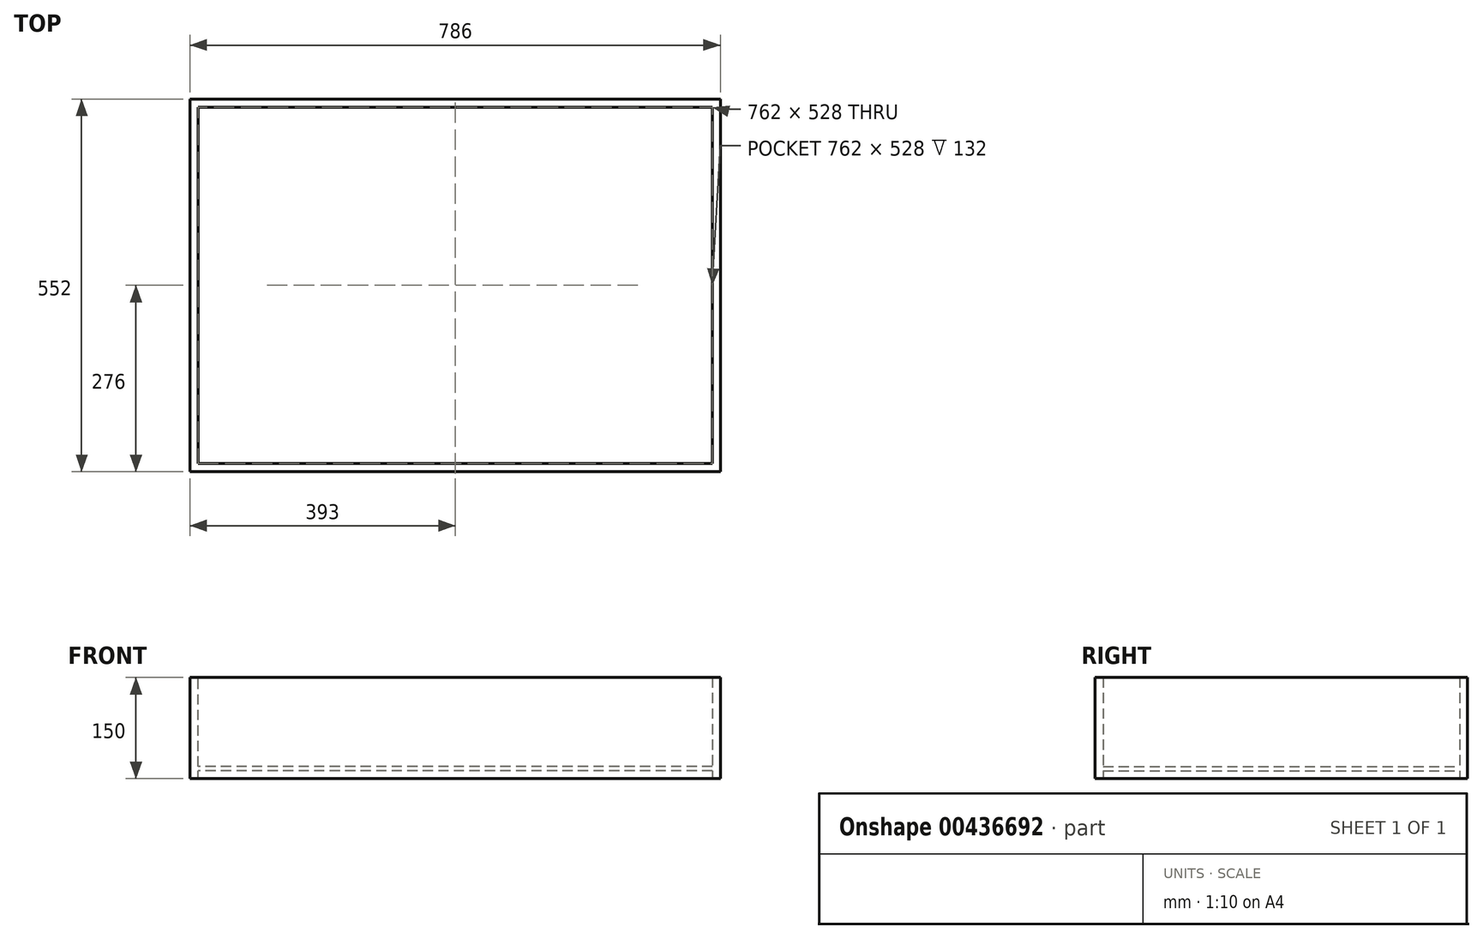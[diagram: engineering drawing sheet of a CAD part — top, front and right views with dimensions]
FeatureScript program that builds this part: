
annotation { "Feature Type Name" : "Feature", "Feature Type Description" : "" }
export const myFeature = defineFeature(function(context is Context, id is Id, definition is map)
    precondition{}
    {
        {
            var Q0;
            Q0=qCreatedBy(makeId("Front.planeOp"),FACE);
            var sketch = newSketch(context, id + "F0", { "sketchPlane" : qUnion([Q0])});
            skLineSegment(sketch, "E0.bottom", {"start": v(381, 3) * mm, "end": v(-381, 3) * mm});
            skLineSegment(sketch, "E0.top", {"start": v(381, -3) * mm, "end": v(-381, -3) * mm});
            skPoint(sketch, "E0.middle", {"position": v(0, 0) * mm});
            skLineSegment(sketch, "E1.bottom", {"start": v(-381, 135) * mm, "end": v(-393, 135) * mm});
            skLineSegment(sketch, "E1.top", {"start": v(-381, -15) * mm, "end": v(-393, -15) * mm});
            skLineSegment(sketch, "E1.left", {"start": v(-381, 135) * mm, "end": v(-381, 3) * mm});
            skLineSegment(sketch, "E1.right", {"start": v(-393, 135) * mm, "end": v(-393, -15) * mm});
            skLineSegment(sketch, "E2.bottom", {"start": v(381, 135) * mm, "end": v(393, 135) * mm});
            skLineSegment(sketch, "E2.top", {"start": v(381, -15) * mm, "end": v(393, -15) * mm});
            skLineSegment(sketch, "E2.left", {"start": v(381, 135) * mm, "end": v(381, 3) * mm});
            skLineSegment(sketch, "E2.right", {"start": v(393, 135) * mm, "end": v(393, -15) * mm});
            skLineSegment(sketch, "E3.trimOffspring", {"start": v(-381, -3) * mm, "end": v(-381, -15) * mm});
            skLineSegment(sketch, "E4.trimOffspring", {"start": v(381, -3) * mm, "end": v(381, -15) * mm});
            skSolve(sketch);
        }
        {
            var Q0;
            Q0=qSketchRegion(id+"F0",true);
            extrude(context, id + "F1", {"entities" : qUnion([Q0]), "depth" : 552 * mm});
        }
        {
            var Q0;
            Q0=makeQuery(id+"F1.opExtrude","SWEPT_FACE",FACE,{"disambiguationData":[OSD([sQuery(id+"F0.wireOp",EDGE,"E2.left")])]});
            var sketch = newSketch(context, id + "F2", { "sketchPlane" : qUnion([Q0])});
            skLineSegment(sketch, "E5.bottom", {"start": v(0, 135) * mm, "end": v(12, 135) * mm});
            skLineSegment(sketch, "E5.top", {"start": v(0, -15) * mm, "end": v(12, -15) * mm});
            skLineSegment(sketch, "E5.left", {"start": v(0, 135) * mm, "end": v(0, -15) * mm});
            skLineSegment(sketch, "E5.right", {"start": v(12, 135) * mm, "end": v(12, -15) * mm});
            skLineSegment(sketch, "E6.bottom", {"start": v(552, 135) * mm, "end": v(540, 135) * mm});
            skLineSegment(sketch, "E6.top", {"start": v(552, -15) * mm, "end": v(540, -15) * mm});
            skLineSegment(sketch, "E6.left", {"start": v(552, 135) * mm, "end": v(552, -15) * mm});
            skLineSegment(sketch, "E6.right", {"start": v(540, 135) * mm, "end": v(540, -15) * mm});
            skSolve(sketch);
        }
        {
            var Q0;
            Q0=qSketchRegion(id+"F2",true);
            var Q1;
            Q1=makeQuery(id+"F1.opExtrude","SWEPT_FACE",FACE,{"disambiguationData":[OSD([sQuery(id+"F0.wireOp",EDGE,"E1.left")])]});
            extrude(context, id + "F3", {"entities" : qUnion([Q0]), "operationType" : NewBodyOperationType.ADD, "endBound" : BoundingType.UP_TO_SURFACE, "endBoundEntityFace" : qUnion([Q1]), "depth" : 520 * mm});
        }
    });
